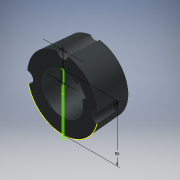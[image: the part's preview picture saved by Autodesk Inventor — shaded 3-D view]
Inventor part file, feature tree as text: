
AUTODESK INVENTOR PART (.ipt)
format: ipt  version: 2018 (Build 220112000, 112)  size: 198,144 bytes
history: native  units: mm
features: sketch x9, extrude x6, hole x2, other x2
ambient origin geometry x8: Origin, YZ Plane, XZ Plane, XY Plane, X Axis, Y Axis, Z Axis, Center Point
bodies: Solido1 (feature_tree)
feature tree (19):
  extrude  "Estrusione1"  Depth=30.0mm
  extrude  "Estrusione2"  Depth=80.0mm
  hole  "Foro1"  [1 undecoded]
  hole  "Foro2"  [1 undecoded]
  extrude  "Estrusione3"  Depth=34.0mm TaperAngle=0.0deg
  extrude  "Estrusione4"  Depth=69.77mm
  extrude  "Estrusione5"  Depth=16.580628mm
  other  "Sformo faccia1"
  extrude  "Estrusione6"  Depth=16.580628mm
  sketch  "Schizzo9"
  sketch  "Schizzo1"
  sketch  "Schizzo2"
  sketch  "Schizzo3"
  sketch  "Schizzo4"
  sketch  "Schizzo5"
  sketch  "Schizzo6"
  other  "Linea chiusa proiettata1"
  sketch  "Schizzo7"
  sketch  "Schizzo8"
note: 2 required parameter values undecoded (feature->parameter linkage not recoverable at this tier; creation-order binding heuristic only, values carry confidence <= 0.55)
